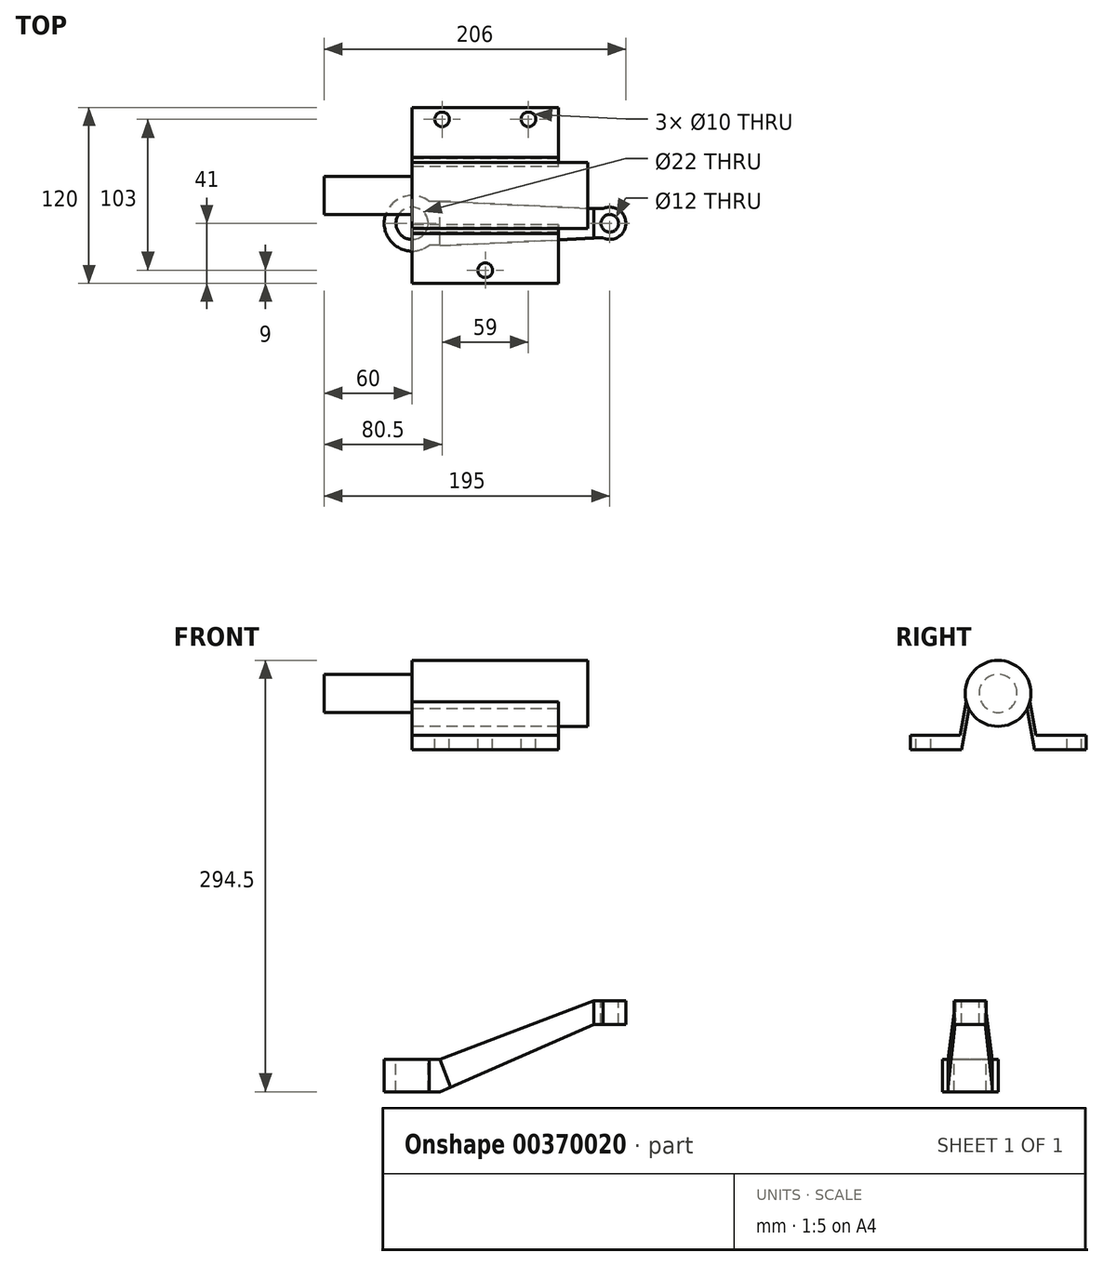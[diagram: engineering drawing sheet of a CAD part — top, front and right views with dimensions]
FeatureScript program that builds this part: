
annotation { "Feature Type Name" : "Feature", "Feature Type Description" : "" }
export const myFeature = defineFeature(function(context is Context, id is Id, definition is map)
    precondition{}
    {
        {
            var Q0;
            Q0=qCreatedBy(makeId("Front.planeOp"),FACE);
            var sketch = newSketch(context, id + "F0", { "sketchPlane" : qUnion([Q0])});
            skLineSegment(sketch, "E0", {"start": v(0, 0) * mm, "end": v(120, 0) * mm});
            skLineSegment(sketch, "E1", {"start": v(120, 0) * mm, "end": v(120, 22.5) * mm});
            skLineSegment(sketch, "E2", {"start": v(120, 22.5) * mm, "end": v(0, 22.5) * mm});
            skLineSegment(sketch, "E3", {"start": v(0, 22.5) * mm, "end": v(0, 0) * mm});
            skPoint(sketch, "E4", {"position": v(0, 13) * mm});
            skLineSegment(sketch, "E5", {"start": v(0, 13) * mm, "end": v(-60, 13) * mm});
            skLineSegment(sketch, "E6", {"start": v(-60, 13) * mm, "end": v(-60, 0) * mm});
            skLineSegment(sketch, "E7", {"start": v(-60, 0) * mm, "end": v(0, 0) * mm});
            skSolve(sketch);
        }
        {
            var Q0;
            {var subQ3=sQuery(id+"F0.wireOp",EDGE,"E0");Q0=makeQuery(id+"F0.imprint","IMPRINT",FACE,{"disambiguationData":[TD([[makeQuery(id+"F0.imprint","IMPRINT",EDGE,{"derivedFrom":subQ3}),1.0]])]});}
            var Q1;
            Q1=sQuery(id+"F0.wireOp",EDGE,"E0");
            revolve(context, id + "F1", {"entities" : qUnion([Q0]), "axis" : qUnion([Q1]), "revolveType" : RevolveType.FULL});
        }
        {
            var Q0;
            Q0=qCreatedBy(makeId("Right.planeOp"),FACE);
            var sketch = newSketch(context, id + "F2", { "sketchPlane" : qUnion([Q0])});
            skCircle(sketch, "E8.0", {"center": v(0, 0) * mm, "radius": 22.5 * mm});
            skPoint(sketch, "E9", {"position": v(22.5, 0) * mm});
            skPoint(sketch, "E10", {"position": v(19.86, -10.58) * mm});
            skPoint(sketch, "E11", {"position": v(-20.14, -10.02) * mm});
            skPoint(sketch, "E12", {"position": v(0, -22.5) * mm});
            skPoint(sketch, "E13", {"position": v(0, -10.58) * mm});
            skPoint(sketch, "E14", {"position": v(25, -38.58) * mm});
            skLineSegment(sketch, "E15", {"start": v(19.86, -10.58) * mm, "end": v(25, -38.58) * mm});
            skPoint(sketch, "E16", {"position": v(19.86, -5.58) * mm});
            skLineSegment(sketch, "E17", {"start": v(19.86, -5.58) * mm, "end": v(21.8, -5.58) * mm});
            skLineSegment(sketch, "E18", {"start": v(21.8, -5.58) * mm, "end": v(26.02, -28.58) * mm});
            skLineSegment(sketch, "E19", {"start": v(25, -38.58) * mm, "end": v(60, -38.58) * mm});
            skLineSegment(sketch, "E20", {"start": v(60, -38.58) * mm, "end": v(60, -28.58) * mm});
            skLineSegment(sketch, "E21", {"start": v(60, -28.58) * mm, "end": v(26.02, -28.58) * mm});
            skPoint(sketch, "E22.orphan", {"position": v(26.04, -28.66) * mm});
            skLineSegment(sketch, "E23", {"start": v(0, 22.5) * mm, "end": v(0, -22.5) * mm, "construction": true});
            skLineSegment(sketch, "E24.MirrorCS", {"start": v(-19.86, -10.58) * mm, "end": v(-25, -38.58) * mm});
            skLineSegment(sketch, "E25.MirrorCS", {"start": v(-21.8, -5.58) * mm, "end": v(-26.02, -28.58) * mm});
            skLineSegment(sketch, "E26.MirrorCS", {"start": v(-60, -28.58) * mm, "end": v(-26.02, -28.58) * mm});
            skLineSegment(sketch, "E27.MirrorCS", {"start": v(-60, -38.58) * mm, "end": v(-60, -28.58) * mm});
            skLineSegment(sketch, "E28.MirrorCS", {"start": v(-25, -38.58) * mm, "end": v(-60, -38.58) * mm});
            skSolve(sketch);
        }
        {
            var Q0;
            Q0=qSketchRegion(id+"F2",true);
            extrude(context, id + "F3", {"entities" : qUnion([Q0]), "operationType" : NewBodyOperationType.ADD, "depth" : 100 * mm});
        }
        {
            var Q0;
            Q0=makeQuery(id+"F3.opExtrude","SWEPT_FACE",FACE,{"disambiguationData":[OSD([sQuery(id+"F2.wireOp",EDGE,"E21")])]});
            var sketch = newSketch(context, id + "F4", { "sketchPlane" : qUnion([Q0])});
            skLineSegment(sketch, "E29.0", {"start": v(100, -60) * mm, "end": v(0, -60) * mm});
            skPoint(sketch, "E30", {"position": v(50, -51) * mm});
            skPoint(sketch, "E30.positionSnap0", {"position": v(50, -60) * mm});
            skPoint(sketch, "E31", {"position": v(50, 52) * mm});
            skPoint(sketch, "E31.positionSnap0", {"position": v(50, 60) * mm});
            skPoint(sketch, "E32", {"position": v(79.5, 52) * mm});
            skPoint(sketch, "E33", {"position": v(20.5, 52) * mm});
            skCircle(sketch, "E34", {"center": v(20.5, 52) * mm, "radius": 5 * mm});
            skCircle(sketch, "E35", {"center": v(79.5, 52) * mm, "radius": 5 * mm});
            skCircle(sketch, "E36", {"center": v(50, -51) * mm, "radius": 5 * mm});
            skSolve(sketch);
        }
        {
            var Q0;
            Q0=qSketchRegion(id+"F4",true);
            extrude(context, id + "F5", {"entities" : qUnion([Q0]), "operationType" : NewBodyOperationType.REMOVE, "oppositeDirection" : true, "depth" : 10 * mm});
        }
        {
            var Q0;
            Q0=qCreatedBy(makeId("Front.planeOp"),FACE);
            var sketch = newSketch(context, id + "F6", { "sketchPlane" : qUnion([Q0])});
            skPoint(sketch, "E37", {"position": v(0, -250) * mm});
            skPoint(sketch, "E38", {"position": v(135, -210) * mm});
            skLineSegment(sketch, "E39", {"start": v(0, -250) * mm, "end": v(-19, -250) * mm});
            skLineSegment(sketch, "E40", {"start": v(-19, -250) * mm, "end": v(-19, -272) * mm});
            skLineSegment(sketch, "E41", {"start": v(-19, -272) * mm, "end": v(19, -272) * mm});
            skLineSegment(sketch, "E42", {"start": v(19, -272) * mm, "end": v(19, -250) * mm});
            skLineSegment(sketch, "E43", {"start": v(19, -250) * mm, "end": v(0, -250) * mm});
            skLineSegment(sketch, "E44", {"start": v(135, -210) * mm, "end": v(135, -226) * mm});
            skLineSegment(sketch, "E45", {"start": v(135, -210) * mm, "end": v(124, -210) * mm});
            skLineSegment(sketch, "E46", {"start": v(124, -210) * mm, "end": v(124, -226) * mm});
            skLineSegment(sketch, "E47", {"start": v(124, -226) * mm, "end": v(135, -226) * mm});
            skLineSegment(sketch, "E48", {"start": v(135, -210) * mm, "end": v(146, -210) * mm});
            skLineSegment(sketch, "E49", {"start": v(146, -210) * mm, "end": v(146, -226) * mm});
            skLineSegment(sketch, "E50", {"start": v(146, -226) * mm, "end": v(135, -226) * mm});
            skLineSegment(sketch, "E51", {"start": v(19, -250) * mm, "end": v(124, -210) * mm});
            skLineSegment(sketch, "E52", {"start": v(19, -272) * mm, "end": v(124, -226) * mm});
            skSolve(sketch);
        }
        {
            var Q0;
            Q0=qSketchRegion(id+"F6",true);
            extrude(context, id + "F7", {"entities" : qUnion([Q0]), "depth" : 38 * mm});
        }
        {
            var Q0;
            Q0=makeQuery(id+"F7.opExtrude","SWEPT_FACE",FACE,{"disambiguationData":[OSD([sQuery(id+"F6.wireOp",EDGE,"E39"),sQuery(id+"F6.wireOp",EDGE,"E43")])]});
            var sketch = newSketch(context, id + "F8", { "sketchPlane" : qUnion([Q0])});
            skPoint(sketch, "E53", {"position": v(0, -19) * mm});
            skPoint(sketch, "E53.positionSnap0", {"position": v(-19, -19) * mm});
            skCircle(sketch, "E54", {"center": v(0, -19) * mm, "radius": 11 * mm});
            skCircle(sketch, "E55", {"center": v(0, -19) * mm, "radius": 19 * mm});
            skLineSegment(sketch, "E56.0", {"start": v(19, 0) * mm, "end": v(-19, 0) * mm});
            skLineSegment(sketch, "E57.0", {"start": v(19, -38) * mm, "end": v(19, 0) * mm});
            skLineSegment(sketch, "E58.0", {"start": v(19, -38) * mm, "end": v(-19, -38) * mm});
            skLineSegment(sketch, "E59.0", {"start": v(-19, -38) * mm, "end": v(-19, 0) * mm});
            skLineSegment(sketch, "E60", {"start": v(19, -19) * mm, "end": v(19, -4) * mm});
            skLineSegment(sketch, "E61", {"start": v(19, -4) * mm, "end": v(11.66, -4) * mm});
            skLineSegment(sketch, "E62", {"start": v(19, -19) * mm, "end": v(19, -34) * mm});
            skLineSegment(sketch, "E63", {"start": v(19, -34) * mm, "end": v(11.66, -34) * mm});
            skSolve(sketch);
        }
        {
            var Q0;
            Q0=makeQuery(id+"F8.imprint","IMPRINT",FACE,{"disambiguationData":[TD([[makeQuery(id+"F8.imprint","IMPRINT",EDGE,{"derivedFrom":sQuery(id+"F8.wireOp",EDGE,"E54")}),1.0]])]});
            var Q1;
            {var subQ0=sQuery(id+"F8.wireOp",EDGE,"E56.0");var subQ1=sQuery(id+"F8.wireOp",EDGE,"E55");var subQ2=makeQuery(id+"F8.imprint","INTERSECT",VERTEX,{"derivedFrom":[subQ1,subQ0]});Q1=makeQuery(id+"F8.imprint","IMPRINT",FACE,{"disambiguationData":[TD([[makeQuery(id+"F8.imprint","IMPRINT",EDGE,{"disambiguationData":[TD([[subQ2,-1.0]])],"derivedFrom":subQ1}),-1.0]])]});}
            var Q2;
            {var subQ0=sQuery(id+"F8.wireOp",EDGE,"E61");Q2=makeQuery(id+"F8.imprint","IMPRINT",FACE,{"disambiguationData":[TD([[makeQuery(id+"F8.imprint","IMPRINT",EDGE,{"derivedFrom":subQ0}),-1.0]])]});}
            var Q3;
            {var subQ0=sQuery(id+"F8.wireOp",EDGE,"E63");Q3=makeQuery(id+"F8.imprint","IMPRINT",FACE,{"disambiguationData":[TD([[makeQuery(id+"F8.imprint","IMPRINT",EDGE,{"derivedFrom":subQ0}),1.0]])]});}
            var Q4;
            {var subQ0=sQuery(id+"F8.wireOp",EDGE,"E59.0");var subQ1=sQuery(id+"F8.wireOp",EDGE,"E55");var subQ2=makeQuery(id+"F8.imprint","INTERSECT",VERTEX,{"derivedFrom":[subQ1,subQ0]});Q4=makeQuery(id+"F8.imprint","IMPRINT",FACE,{"disambiguationData":[TD([[makeQuery(id+"F8.imprint","IMPRINT",EDGE,{"disambiguationData":[TD([[subQ2,-1.0]])],"derivedFrom":subQ1}),-1.0]])]});}
            extrude(context, id + "F9", {"entities" : qUnion([Q0, Q1, Q2, Q3, Q4]), "operationType" : NewBodyOperationType.REMOVE, "oppositeDirection" : true, "depth" : 25 * mm});
        }
        {
            var Q0;
            Q0=makeQuery(id+"F7.opExtrude","SWEPT_FACE",FACE,{"disambiguationData":[OSD([sQuery(id+"F6.wireOp",EDGE,"E45"),sQuery(id+"F6.wireOp",EDGE,"E48")])]});
            var sketch = newSketch(context, id + "F10", { "sketchPlane" : qUnion([Q0])});
            skPoint(sketch, "E64", {"position": v(135, -19) * mm});
            skPoint(sketch, "E64.positionSnap0", {"position": v(146, -19) * mm});
            skPoint(sketch, "E64.positionSnap1", {"position": v(135, 0) * mm});
            skCircle(sketch, "E65", {"center": v(135, -19) * mm, "radius": 6 * mm});
            skCircle(sketch, "E66", {"center": v(135, -19) * mm, "radius": 11 * mm});
            skLineSegment(sketch, "E67", {"start": v(124, -19) * mm, "end": v(124, -9) * mm});
            skLineSegment(sketch, "E68", {"start": v(124, -19) * mm, "end": v(124, -29) * mm});
            skLineSegment(sketch, "E69", {"start": v(124, -9) * mm, "end": v(130.42, -9) * mm});
            skLineSegment(sketch, "E70", {"start": v(124, -29) * mm, "end": v(130.42, -29) * mm});
            skLineSegment(sketch, "E71.0", {"start": v(124, -38) * mm, "end": v(124, 0) * mm});
            skLineSegment(sketch, "E72.0", {"start": v(124, 0) * mm, "end": v(146, 0) * mm});
            skLineSegment(sketch, "E73.0", {"start": v(146, -38) * mm, "end": v(146, 0) * mm});
            skLineSegment(sketch, "E74.0", {"start": v(124, -38) * mm, "end": v(146, -38) * mm});
            skSolve(sketch);
        }
        {
            var Q0;
            Q0=makeQuery(id+"F10.imprint","IMPRINT",FACE,{"disambiguationData":[TD([[makeQuery(id+"F10.imprint","IMPRINT",EDGE,{"derivedFrom":sQuery(id+"F10.wireOp",EDGE,"E65")}),1.0]])]});
            var Q1;
            {var subQ2=sQuery(id+"F10.wireOp",EDGE,"E69");Q1=makeQuery(id+"F10.imprint","IMPRINT",FACE,{"disambiguationData":[TD([[makeQuery(id+"F10.imprint","IMPRINT",EDGE,{"derivedFrom":subQ2}),1.0]])]});}
            var Q2;
            {var subQ5=sQuery(id+"F10.wireOp",EDGE,"E70");Q2=makeQuery(id+"F10.imprint","IMPRINT",FACE,{"disambiguationData":[TD([[makeQuery(id+"F10.imprint","IMPRINT",EDGE,{"derivedFrom":subQ5}),-1.0]])]});}
            extrude(context, id + "F11", {"entities" : qUnion([Q0, Q1, Q2]), "operationType" : NewBodyOperationType.REMOVE, "oppositeDirection" : true, "depth" : 25 * mm});
        }
        {
            var Q0;
            Q0=makeQuery(id+"F7.opExtrude","SWEPT_FACE",FACE,{"disambiguationData":[OSD([sQuery(id+"F6.wireOp",EDGE,"E51")])]});
            var sketch = newSketch(context, id + "F12", { "sketchPlane" : qUnion([Q0])});
            skLineSegment(sketch, "E75.0", {"start": v(41.12, -29) * mm, "end": v(41.12, -9) * mm});
            skLineSegment(sketch, "E76.0", {"start": v(-71.24, -34) * mm, "end": v(-71.24, -4) * mm});
            skLineSegment(sketch, "E77", {"start": v(-71.24, -34) * mm, "end": v(41.12, -29) * mm});
            skLineSegment(sketch, "E78", {"start": v(-71.24, -4) * mm, "end": v(41.12, -9) * mm});
            skLineSegment(sketch, "E79.0", {"start": v(-71.24, -38) * mm, "end": v(41.12, -38) * mm});
            skLineSegment(sketch, "E80.0", {"start": v(-71.24, 0) * mm, "end": v(41.12, 0) * mm});
            skLineSegment(sketch, "E81", {"start": v(41.12, 0) * mm, "end": v(41.12, -9) * mm});
            skLineSegment(sketch, "E82", {"start": v(41.12, -29) * mm, "end": v(41.12, -38) * mm});
            skLineSegment(sketch, "E83", {"start": v(-71.24, -34) * mm, "end": v(-71.24, -38) * mm});
            skLineSegment(sketch, "E84", {"start": v(-71.24, 0) * mm, "end": v(-71.24, -4) * mm});
            skLineSegment(sketch, "E85", {"start": v(-71.24, -4) * mm, "end": v(-79.24, -4) * mm});
            skLineSegment(sketch, "E86", {"start": v(-79.24, -4) * mm, "end": v(-79.24, 0) * mm});
            skLineSegment(sketch, "E87", {"start": v(-79.24, 0) * mm, "end": v(-71.24, 0) * mm});
            skLineSegment(sketch, "E88", {"start": v(-71.24, -38) * mm, "end": v(-79.24, -38) * mm});
            skLineSegment(sketch, "E89", {"start": v(-79.24, -38) * mm, "end": v(-79.24, -34) * mm});
            skLineSegment(sketch, "E90", {"start": v(-79.24, -34) * mm, "end": v(-71.24, -34) * mm});
            skSolve(sketch);
        }
        {
            var Q0;
            Q0=makeQuery(id+"F12.imprint","IMPRINT",FACE,{"disambiguationData":[TD([[makeQuery(id+"F12.imprint","IMPRINT",EDGE,{"derivedFrom":sQuery(id+"F12.wireOp",EDGE,"E83")}),1.0]])]});
            var Q1;
            Q1=makeQuery(id+"F12.imprint","IMPRINT",FACE,{"disambiguationData":[TD([[makeQuery(id+"F12.imprint","IMPRINT",EDGE,{"derivedFrom":sQuery(id+"F12.wireOp",EDGE,"E84")}),1.0]])]});
            var Q2;
            Q2=makeQuery(id+"F12.imprint","IMPRINT",FACE,{"disambiguationData":[TD([[makeQuery(id+"F12.imprint","IMPRINT",EDGE,{"derivedFrom":sQuery(id+"F12.wireOp",EDGE,"E77")}),-1.0]])]});
            var Q3;
            Q3=makeQuery(id+"F12.imprint","IMPRINT",FACE,{"disambiguationData":[TD([[makeQuery(id+"F12.imprint","IMPRINT",EDGE,{"derivedFrom":sQuery(id+"F12.wireOp",EDGE,"E78")}),1.0]])]});
            extrude(context, id + "F13", {"entities" : qUnion([Q0, Q1, Q2, Q3]), "operationType" : NewBodyOperationType.REMOVE, "oppositeDirection" : true, "depth" : 25 * mm});
        }
        {
            var Q0;
            {var subQ2=sQuery(id+"F0.wireOp",EDGE,"E5");Q0=makeQuery(id+"F0.imprint","IMPRINT",FACE,{"disambiguationData":[TD([[makeQuery(id+"F0.imprint","IMPRINT",EDGE,{"derivedFrom":subQ2}),1.0]])]});}
            var Q1;
            Q1=sQuery(id+"F0.wireOp",EDGE,"E7");
            revolve(context, id + "F14", {"entities" : qUnion([Q0]), "axis" : qUnion([Q1]), "revolveType" : RevolveType.FULL});
        }
    });
